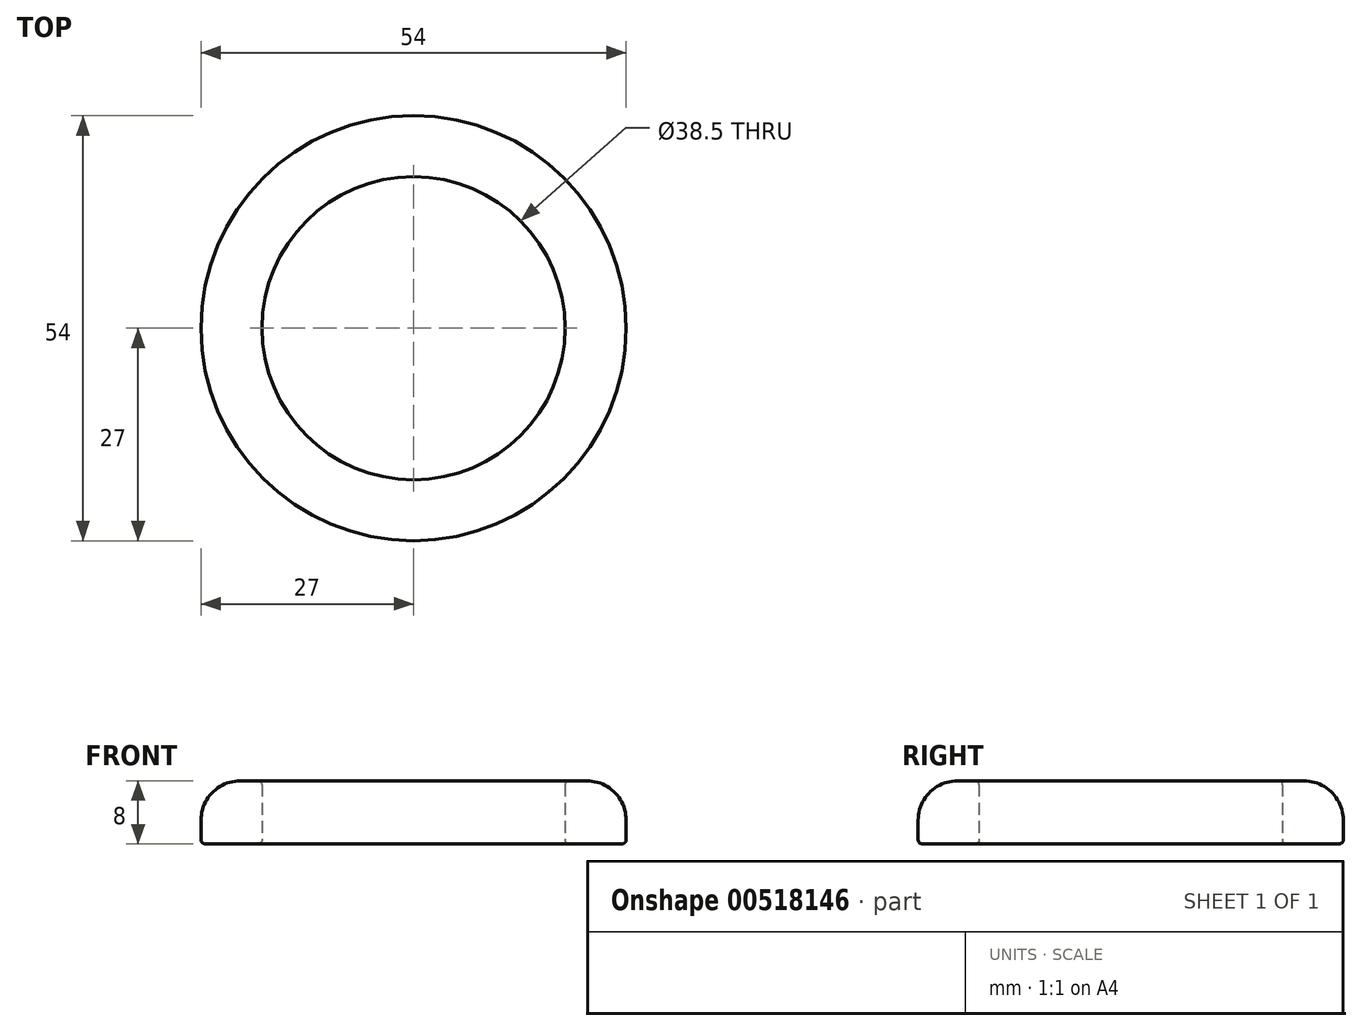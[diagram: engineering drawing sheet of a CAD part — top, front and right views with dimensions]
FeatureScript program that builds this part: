
annotation { "Feature Type Name" : "Feature", "Feature Type Description" : "" }
export const myFeature = defineFeature(function(context is Context, id is Id, definition is map)
    precondition{}
    {
        {
            var Q0;
            Q0=qCreatedBy(makeId("Top.planeOp"),FACE);
            var sketch = newSketch(context, id + "F0", { "sketchPlane" : qUnion([Q0])});
            skCircle(sketch, "E0", {"center": v(0, 0) * mm, "radius": 27 * mm});
            skCircle(sketch, "E1", {"center": v(0, 0) * mm, "radius": 19.25 * mm});
            skSolve(sketch);
        }
        {
            var Q0;
            Q0 = qSketchRegion(id + "F0", true);
            extrude(context, id + "F1", {"entities" : qUnion([Q0]), "depth" : 8 * mm, "offsetDistance" : 25 * mm});
        }
        {
            var Q0;
            Q0=makeQuery(id+"F1.opExtrude","CAP_EDGE",EDGE,{"disambiguationData":[OSD([sQuery(id+"F0.wireOp",EDGE,"E0")])],"isStart":false});
            fillet(context, id + "F2", {"entities" : qUnion([Q0]), "radius" : 5 * mm, "tangentPropagation" : true, "allowEdgeOverflow" : false});
        }
        {
            var Q0;
            Q0=makeQuery(id+"F1.opExtrude","CAP_EDGE",EDGE,{"disambiguationData":[OSD([sQuery(id+"F0.wireOp",EDGE,"E1")])],"isStart":false});
            var Q1;
            Q1=makeQuery(id+"F1.opExtrude","CAP_EDGE",EDGE,{"disambiguationData":[OSD([sQuery(id+"F0.wireOp",EDGE,"E1")])],"isStart":true});
            fillet(context, id + "F3", {"entities" : qUnion([Q0, Q1]), "radius" : 0.5 * mm, "tangentPropagation" : true, "allowEdgeOverflow" : false});
        }
        {
            var Q0;
            Q0=makeQuery(id+"F1.opExtrude","CAP_EDGE",EDGE,{"disambiguationData":[OSD([sQuery(id+"F0.wireOp",EDGE,"E0")])],"isStart":true});
            fillet(context, id + "F4", {"entities" : qUnion([Q0]), "radius" : 0.5 * mm, "tangentPropagation" : true, "allowEdgeOverflow" : false});
        }
    });
